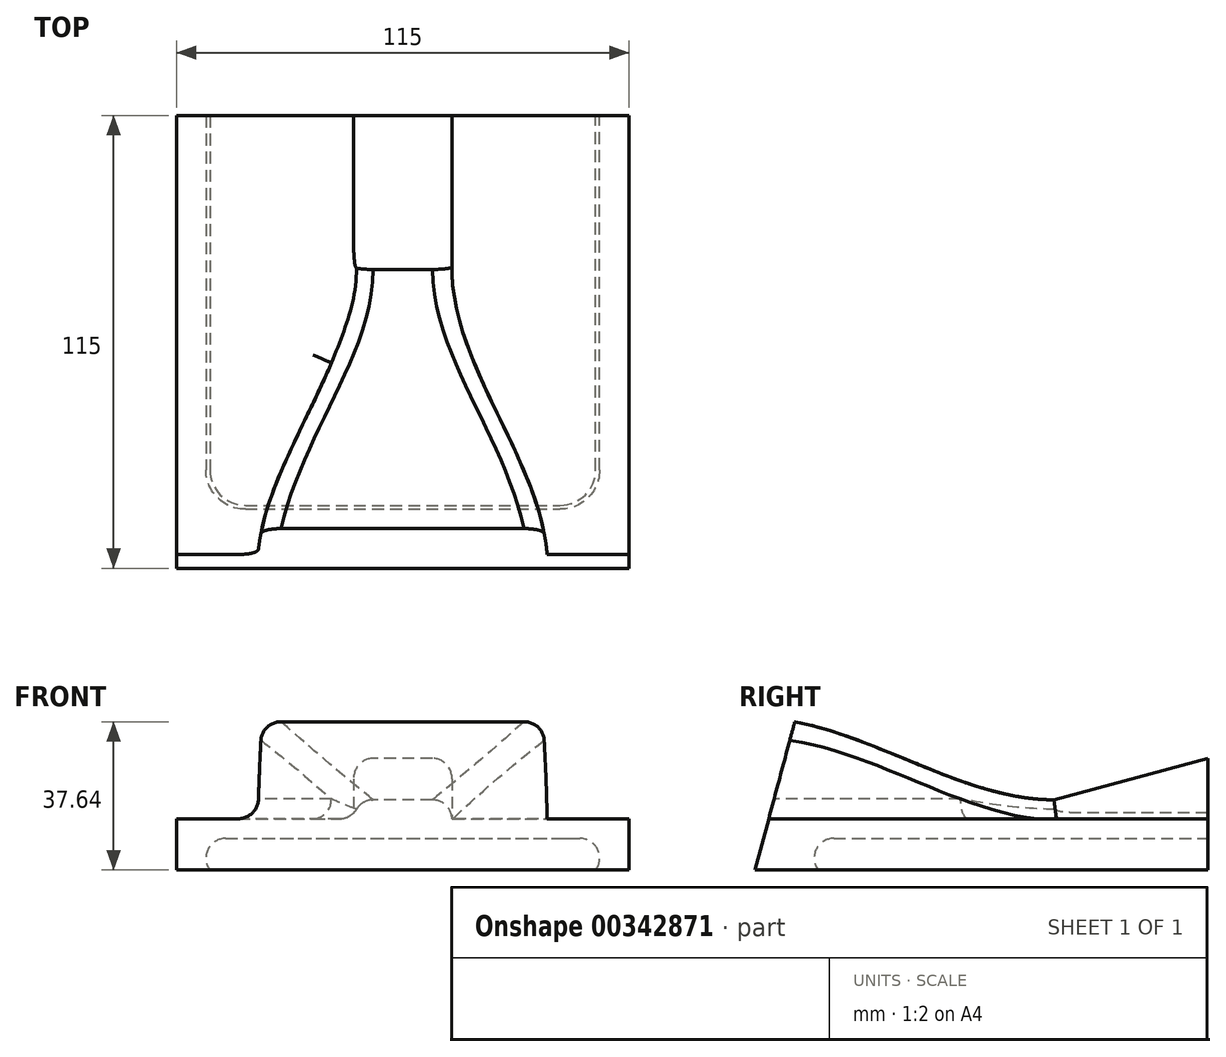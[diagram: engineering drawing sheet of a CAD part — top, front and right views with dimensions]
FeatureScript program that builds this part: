
annotation { "Feature Type Name" : "Feature", "Feature Type Description" : "" }
export const myFeature = defineFeature(function(context is Context, id is Id, definition is map)
    precondition{}
    {
        {
            var Q0;
            Q0=qCreatedBy(makeId("Front.planeOp"),FACE);
            var sketch = newSketch(context, id + "F0", { "sketchPlane" : qUnion([Q0])});
            skLineSegment(sketch, "E0.bottom", {"start": v(50, -5) * mm, "end": v(-50, -5) * mm});
            skLineSegment(sketch, "E0.top", {"start": v(50, 5) * mm, "end": v(-50, 5) * mm});
            skLineSegment(sketch, "E0.left", {"start": v(50, -5) * mm, "end": v(50, 5) * mm});
            skLineSegment(sketch, "E0.right", {"start": v(-50, -5) * mm, "end": v(-50, 5) * mm});
            skPoint(sketch, "E0.middle", {"position": v(0, 0) * mm});
            skSolve(sketch);
        }
        {
            var Q0;
            Q0 = qSketchRegion(id + "F0", true);
            extrude(context, id + "F1", {"entities" : qUnion([Q0]), "endBound" : BoundingType.SYMMETRIC, "depth" : 200 * mm});
        }
        {
            var Q0;
            Q0=qCreatedBy(makeId("Top.planeOp"),FACE);
            var sketch = newSketch(context, id + "F2", { "sketchPlane" : qUnion([Q0])});
            skLineSegment(sketch, "E1.bottom", {"start": v(40, 100) * mm, "end": v(-40, 100) * mm});
            skLineSegment(sketch, "E1.top", {"start": v(40, -100) * mm, "end": v(-40, -100) * mm});
            skLineSegment(sketch, "E1.left", {"start": v(50, 90) * mm, "end": v(50, -90) * mm});
            skLineSegment(sketch, "E1.right", {"start": v(-50, 90) * mm, "end": v(-50, -90) * mm});
            skPoint(sketch, "E1.middle", {"position": v(0, 0) * mm});
            skPoint(sketch, "E2.visualSharp", {"position": v(50, 100) * mm});
            skPoint(sketch, "E3.visualSharp", {"position": v(50, -100) * mm});
            skPoint(sketch, "E4.visualSharp", {"position": v(-50, -100) * mm});
            skArc(sketch, "E5", {"start": v(50, 90) * mm, "mid": v(47.07, 97.07) * mm, "end": v(40, 100) * mm});
            skArc(sketch, "E6", {"start": v(-40, 100) * mm, "mid": v(-47.07, 97.07) * mm, "end": v(-50, 90) * mm});
            skArc(sketch, "E7", {"start": v(40, -100) * mm, "mid": v(47.07, -97.07) * mm, "end": v(50, -90) * mm});
            skArc(sketch, "E8", {"start": v(-50, -90) * mm, "mid": v(-47.07, -97.07) * mm, "end": v(-40, -100) * mm});
            skSolve(sketch);
        }
        {
            var Q0;
            Q0=makeQuery(id+"F1.opExtrude","SWEPT_FACE",FACE,{"disambiguationData":[OSD([sQuery(id+"F0.wireOp",EDGE,"E0.left")])]});
            var sketch = newSketch(context, id + "F3", { "sketchPlane" : qUnion([Q0])});
            skLineSegment(sketch, "E9", {"start": v(0, -5) * mm, "end": v(0, 5) * mm, "construction": true});
            skSolve(sketch);
        }
        {
            var Q0;
            Q0=makeQuery(id+"F1.opExtrude","SWEPT_FACE",FACE,{"disambiguationData":[OSD([sQuery(id+"F0.wireOp",EDGE,"E0.bottom")])]});
            var sketch = newSketch(context, id + "F4", { "sketchPlane" : qUnion([Q0])});
            skLineSegment(sketch, "E10", {"start": v(50, 0) * mm, "end": v(-50, 0) * mm, "construction": true});
            skLineSegment(sketch, "E11", {"start": v(0, 100) * mm, "end": v(0, -100) * mm, "construction": true});
            skSolve(sketch);
        }
        {
            var Q0;
            Q0=makeQuery(id+"F1.opExtrude","CAP_FACE",FACE,{"disambiguationData":[OSD([sQuery(id+"F0.wireOp",EDGE,"E0.bottom"),sQuery(id+"F0.wireOp",EDGE,"E0.top"),sQuery(id+"F0.wireOp",EDGE,"E0.left"),sQuery(id+"F0.wireOp",EDGE,"E0.right")])],"isStart":false});
            var Q1;
            Q1=sQuery(id+"F2.wireOp",VERTEX,"E1.left.end");
            cPlane(context, id + "F5", {"entities" : qUnion([Q0, Q1]), "cplaneType" : CPlaneType.PLANE_POINT, "offset" : 25 * mm, "width" : 150 * mm, "height" : 150 * mm});
        }
        {
            var Q0;
            Q0=qCreatedBy(id+"F5.planeOp",FACE);
            var sketch = newSketch(context, id + "F6", { "sketchPlane" : qUnion([Q0])});
            skArc(sketch, "E12", {"start": v(45, -5) * mm, "mid": v(50, 0) * mm, "end": v(45, 5) * mm});
            skLineSegment(sketch, "E13", {"start": v(45, 5) * mm, "end": v(60, 5) * mm});
            skLineSegment(sketch, "E14", {"start": v(60, 5) * mm, "end": v(60, -5) * mm});
            skLineSegment(sketch, "E15", {"start": v(60, -5) * mm, "end": v(45, -5) * mm});
            skSolve(sketch);
        }
        {
            var Q0;
            Q0=makeQuery(id+"F6.imprint","IMPRINT",FACE,{"disambiguationData":[TD([[makeQuery(id+"F6.imprint","IMPRINT",EDGE,{"derivedFrom":sQuery(id+"F6.wireOp",EDGE,"E12")}),-1.0]])]});
            var Q1;
            Q1 = qConstructionFilter(qBodyType(qCreatedBy(id + "F2" ,EDGE), BodyType.WIRE), ConstructionObject.NO);
            sweep(context, id + "F7", {"operationType" : NewBodyOperationType.REMOVE, "profiles" : qUnion([Q0]), "path" : qUnion([Q1])});
        }
        {
            var Q0;
            Q0=qCreatedBy(makeId("Front.planeOp"),FACE);
            var sketch = newSketch(context, id + "F8", { "sketchPlane" : qUnion([Q0])});
            skLineSegment(sketch, "E16.bottom", {"start": v(57.5, -10) * mm, "end": v(-57.5, -10) * mm});
            skLineSegment(sketch, "E16.top", {"start": v(57.5, 10) * mm, "end": v(-57.5, 10) * mm});
            skLineSegment(sketch, "E16.left", {"start": v(57.5, -10) * mm, "end": v(57.5, 10) * mm});
            skLineSegment(sketch, "E16.right", {"start": v(-57.5, -10) * mm, "end": v(-57.5, 10) * mm});
            skPoint(sketch, "E16.middle", {"position": v(0, 0) * mm});
            skSolve(sketch);
        }
        {
            var Q0;
            Q0 = qSketchRegion(id + "F8", true);
            extrude(context, id + "F9", {"entities" : qUnion([Q0]), "depth" : 115 * mm});
        }
        {
            var Q0;
            Q0=makeQuery(id+"F1.opExtrude","SWEPT_BODY",BODY,{"disambiguationData":[OSD([sQuery(id+"F0.wireOp",EDGE,"E0.bottom"),sQuery(id+"F0.wireOp",EDGE,"E0.top"),sQuery(id+"F0.wireOp",EDGE,"E0.left"),sQuery(id+"F0.wireOp",EDGE,"E0.right")])]});
            var Q1;
            Q1=makeQuery(id+"F9.opExtrude","SWEPT_BODY",BODY,{"disambiguationData":[OSD([sQuery(id+"F8.wireOp",EDGE,"E16.bottom"),sQuery(id+"F8.wireOp",EDGE,"E16.top"),sQuery(id+"F8.wireOp",EDGE,"E16.left"),sQuery(id+"F8.wireOp",EDGE,"E16.right")])]});
            booleanBodies(context, id + "F10", {"operationType" : BooleanOperationType.SUBTRACTION, "tools" : qUnion([Q0]), "targets" : qUnion([Q1])});
        }
        {
            var Q0;
            Q0=qCreatedBy(makeId("Top.planeOp"),FACE);
            cPlane(context, id + "F11", {"entities" : qUnion([Q0]), "cplaneType" : CPlaneType.OFFSET, "offset" : 3 * mm, "oppositeDirection" : true, "width" : 150 * mm, "height" : 150 * mm});
        }
        {
            var Q0;
            Q0=qCreatedBy(id+"F11.planeOp",FACE);
            var sketch = newSketch(context, id + "F12", { "sketchPlane" : qUnion([Q0])});
            skLineSegment(sketch, "E17.bottom", {"start": v(-65.52, -136.36) * mm, "end": v(66.54, -136.36) * mm});
            skLineSegment(sketch, "E17.top", {"start": v(-65.52, 30.32) * mm, "end": v(66.54, 30.32) * mm});
            skLineSegment(sketch, "E17.left", {"start": v(-65.52, -136.36) * mm, "end": v(-65.52, 30.32) * mm});
            skLineSegment(sketch, "E17.right", {"start": v(66.54, -136.36) * mm, "end": v(66.54, 30.32) * mm});
            skSolve(sketch);
        }
        {
            var Q0;
            Q0=makeQuery(id+"F12.imprint","IMPRINT",FACE,{"disambiguationData":[TD([[makeQuery(id+"F12.imprint","IMPRINT",EDGE,{"derivedFrom":sQuery(id+"F12.wireOp",EDGE,"E17.bottom")}),1.0]])]});
            extrude(context, id + "F13", {"entities" : qUnion([Q0]), "operationType" : NewBodyOperationType.REMOVE, "oppositeDirection" : true, "depth" : 25 * mm});
        }
        {
            var Q0;
            Q0=qCreatedBy(makeId("Right.planeOp"),FACE);
            var sketch = newSketch(context, id + "F14", { "sketchPlane" : qUnion([Q0])});
            skLineSegment(sketch, "E18", {"start": v(-39.08, 10) * mm, "end": v(-39.08, 14.8) * mm});
            skLineSegment(sketch, "E19", {"start": v(-39.08, 14.8) * mm, "end": v(0, 25.34) * mm});
            skLineSegment(sketch, "E20", {"start": v(0, 25.34) * mm, "end": v(0, 10) * mm});
            skLineSegment(sketch, "E21", {"start": v(0, 10) * mm, "end": v(-39.08, 10) * mm});
            skSolve(sketch);
        }
        {
            var Q0;
            Q0 = qSketchRegion(id + "F14", true);
            extrude(context, id + "F15", {"entities" : qUnion([Q0]), "operationType" : NewBodyOperationType.ADD, "endBound" : BoundingType.SYMMETRIC, "depth" : 25 * mm});
        }
        {
            var Q0;
            Q0=makeQuery(id+"F9.opExtrude","CAP_FACE",FACE,{"disambiguationData":[OSD([sQuery(id+"F8.wireOp",EDGE,"E16.bottom"),sQuery(id+"F8.wireOp",EDGE,"E16.top"),sQuery(id+"F8.wireOp",EDGE,"E16.left"),sQuery(id+"F8.wireOp",EDGE,"E16.right")])],"isStart":false});
            cPlane(context, id + "F16", {"entities" : qUnion([Q0]), "cplaneType" : CPlaneType.OFFSET, "offset" : 0 * mm, "width" : 150 * mm, "height" : 150 * mm});
        }
        {
            var Q0;
            Q0=qCreatedBy(id+"F16.planeOp",FACE);
            var sketch = newSketch(context, id + "F17", { "sketchPlane" : qUnion([Q0])});
            skLineSegment(sketch, "E22.bottom", {"start": v(-36.95, 10) * mm, "end": v(36.82, 10) * mm});
            skLineSegment(sketch, "E22.top", {"start": v(-36.95, 35.63) * mm, "end": v(36.82, 35.63) * mm});
            skLineSegment(sketch, "E22.left", {"start": v(-36.95, 10) * mm, "end": v(-36.95, 35.63) * mm});
            skLineSegment(sketch, "E22.right", {"start": v(36.82, 10) * mm, "end": v(36.82, 35.63) * mm});
            skSolve(sketch);
        }
        {
            var Q1;
            Q1=makeQuery(id+"F15.opExtrude","SWEPT_FACE",FACE,{"disambiguationData":[OSD([sQuery(id+"F14.wireOp",EDGE,"E18")])]});
            var Q2;
            Q2=makeQuery(id+"F17.imprint","IMPRINT",FACE,{"disambiguationData":[TD([[makeQuery(id+"F17.imprint","IMPRINT",EDGE,{"derivedFrom":sQuery(id+"F17.wireOp",EDGE,"E22.bottom")}),1.0]])]});
            loft(context, id + "F18", {"operationType" : NewBodyOperationType.ADD, "startCondition" : LoftEndDerivativeType.NORMAL_TO_PROFILE, "startMagnitude" : 1, "endCondition" : LoftEndDerivativeType.NORMAL_TO_PROFILE, "endMagnitude" : 1, "sheetProfilesArray" : [{ "sheetProfileEntities" : qUnion([Q1]) }, { "sheetProfileEntities" : qUnion([Q2]) }]});
        }
        {
            var Q0;
            Q0=makeQuery(id+"F18.opLoft","SWEPT_EDGE",EDGE,{"disambiguationData":[OSD([sQuery(id+"F14.wireOp",EDGE,"E18"),sQuery(id+"F14.wireOp",EDGE,"E19"),sQuery(id+"F17.wireOp",EDGE,"E22.top"),sQuery(id+"F17.wireOp",EDGE,"E22.right")])]});
            var Q1;
            Q1=makeQuery(id+"F18.opLoft","SWEPT_EDGE",EDGE,{"disambiguationData":[OSD([sQuery(id+"F14.wireOp",EDGE,"E18"),sQuery(id+"F14.wireOp",EDGE,"E19"),sQuery(id+"F17.wireOp",EDGE,"E22.top"),sQuery(id+"F17.wireOp",EDGE,"E22.left")])]});
            fillet(context, id + "F19", {"entities" : qUnion([Q0, Q1]), "radius" : 5 * mm, "tangentPropagation" : true, "allowEdgeOverflow" : false});
        }
        {
            var Q0;
            Q0=makeQuery(id+"F15.opExtrude","CAP_EDGE",EDGE,{"disambiguationData":[OSD([sQuery(id+"F14.wireOp",EDGE,"E19")])],"isStart":false});
            var Q1;
            Q1=makeQuery(id+"F15.opExtrude","CAP_EDGE",EDGE,{"disambiguationData":[OSD([sQuery(id+"F14.wireOp",EDGE,"E19")])],"isStart":true});
            fillet(context, id + "F20", {"entities" : qUnion([Q0, Q1]), "radius" : 5 * mm, "tangentPropagation" : true, "allowEdgeOverflow" : false});
        }
        {
            var Q0;
            Q0=makeQuery(id+"F18.opLoft","SWEPT_EDGE",EDGE,{"disambiguationData":[OSD([sQuery(id+"F14.wireOp",EDGE,"E18"),sQuery(id+"F14.wireOp",EDGE,"E21"),sQuery(id+"F17.wireOp",EDGE,"E22.bottom"),sQuery(id+"F17.wireOp",EDGE,"E22.right")])]});
            var Q1;
            Q1=makeQuery(id+"F18.opLoft","SWEPT_EDGE",EDGE,{"disambiguationData":[OSD([sQuery(id+"F14.wireOp",EDGE,"E18"),sQuery(id+"F14.wireOp",EDGE,"E21"),sQuery(id+"F17.wireOp",EDGE,"E22.bottom"),sQuery(id+"F17.wireOp",EDGE,"E22.left")])]});
            fillet(context, id + "F21", {"entities" : qUnion([Q0, Q1]), "radius" : 5 * mm, "tangentPropagation" : true, "allowEdgeOverflow" : false});
        }
        {
            var Q0;
            Q0=qCreatedBy(id+"F16.planeOp",FACE);
            var Q1;
            Q1=makeQuery(id+"F13.boolean.opBoolean","INTERSECT",EDGE,{"derivedFrom":[makeQuery(id+"F9.opExtrude","CAP_FACE",FACE,{"disambiguationData":[OSD([sQuery(id+"F8.wireOp",EDGE,"E16.bottom"),sQuery(id+"F8.wireOp",EDGE,"E16.top"),sQuery(id+"F8.wireOp",EDGE,"E16.left"),sQuery(id+"F8.wireOp",EDGE,"E16.right")])],"isStart":false}),makeQuery(id+"F13.opExtrude","CAP_FACE",FACE,{"disambiguationData":[OSD([sQuery(id+"F12.wireOp",EDGE,"E17.bottom"),sQuery(id+"F12.wireOp",EDGE,"E17.top"),sQuery(id+"F12.wireOp",EDGE,"E17.left"),sQuery(id+"F12.wireOp",EDGE,"E17.right")])],"isStart":true})]});
            cPlane(context, id + "F22", {"entities" : qUnion([Q0, Q1]), "cplaneType" : CPlaneType.LINE_ANGLE, "offset" : 25 * mm, "angle" : 15 * degree, "width" : 150 * mm, "height" : 150 * mm});
        }
        {
            var Q0;
            Q0=qCreatedBy(id+"F22.planeOp",FACE);
            var sketch = newSketch(context, id + "F23", { "sketchPlane" : qUnion([Q0])});
            skLineSegment(sketch, "E23.bottom", {"start": v(73.16, -78.25) * mm, "end": v(-89.62, -78.25) * mm});
            skLineSegment(sketch, "E23.top", {"start": v(73.16, 50.09) * mm, "end": v(-89.62, 50.09) * mm});
            skLineSegment(sketch, "E23.left", {"start": v(73.16, -78.25) * mm, "end": v(73.16, 50.09) * mm});
            skLineSegment(sketch, "E23.right", {"start": v(-89.62, -78.25) * mm, "end": v(-89.62, 50.09) * mm});
            skSolve(sketch);
        }
        {
            var Q0;
            Q0 = qSketchRegion(id + "F23", true);
            extrude(context, id + "F24", {"entities" : qUnion([Q0]), "operationType" : NewBodyOperationType.REMOVE, "oppositeDirection" : true, "depth" : 25 * mm});
        }
    });
